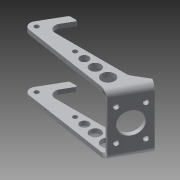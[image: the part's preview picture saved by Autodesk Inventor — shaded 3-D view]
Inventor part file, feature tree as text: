
AUTODESK INVENTOR PART (.ipt)
format: ipt  version: 2013 (Build 170138000, 138)  size: 1,920,000 bytes
history: native  units: in
note: dims shown in document units (in); Inventor stores cm internally (conversion verified against a paired STEP export)
features: sheet_metal_op x4, other x4, sketch x3, mirror x1, chamfer x1
ambient origin geometry x8: Origin, YZ Plane, XZ Plane, XY Plane, X Axis, Y Axis, Z Axis, Center Point
bodies: Solid1 (feature_tree)
feature tree (13):
  sheet_metal_op  "Face1"
  sheet_metal_op  "Flange1"
  mirror  "Mirror1"
  chamfer  "Corner Round1"
  sketch  "Sketch1"  dims[d7=0.375in]
  other  "Plate1"
  sketch  "Sketch2"  dims[d8=0.375in]
  other  "Plate2"
  sheet_metal_op  "Bend1"
  sheet_metal_op  "Corner1"
  sketch  "Sketch3"  dims[d10=0.4278in d11=0.125in d12=0.4722in d13=60.0deg d14=0.7647in d19=1.6084in d20=0.5in d21=0.25in d22=0.25in d23=0.125in d24=0.5in d25=0.25in d26=1.75in d27=90.0deg d28=0.1in d29=1.0in d30=0.25in d31=0.25in d32=2.8in d33=0.266in d34=1.8in d35=2.1084in d36=0.3667in d37=0.7874in d39=1.8in d40=0.7874in d42=1.25in d45=0.25in d46=0.0in d64=1.0in d66=0.5in d67=0.375in d68=0.375in d69=1.9834in d71=4.0549in d72=0.5774in d73=0.6in d74=0.75in d75=0.625in d76=0.5in d77=1.0in d78=1.875in d79=2.625in d80=0.0625in d81=120.0deg d82=1.25in d83=0.266in d84=0.266in d85=3.25in d86=1.25in]
  other  "Cut1"
  other  "Definition1"
